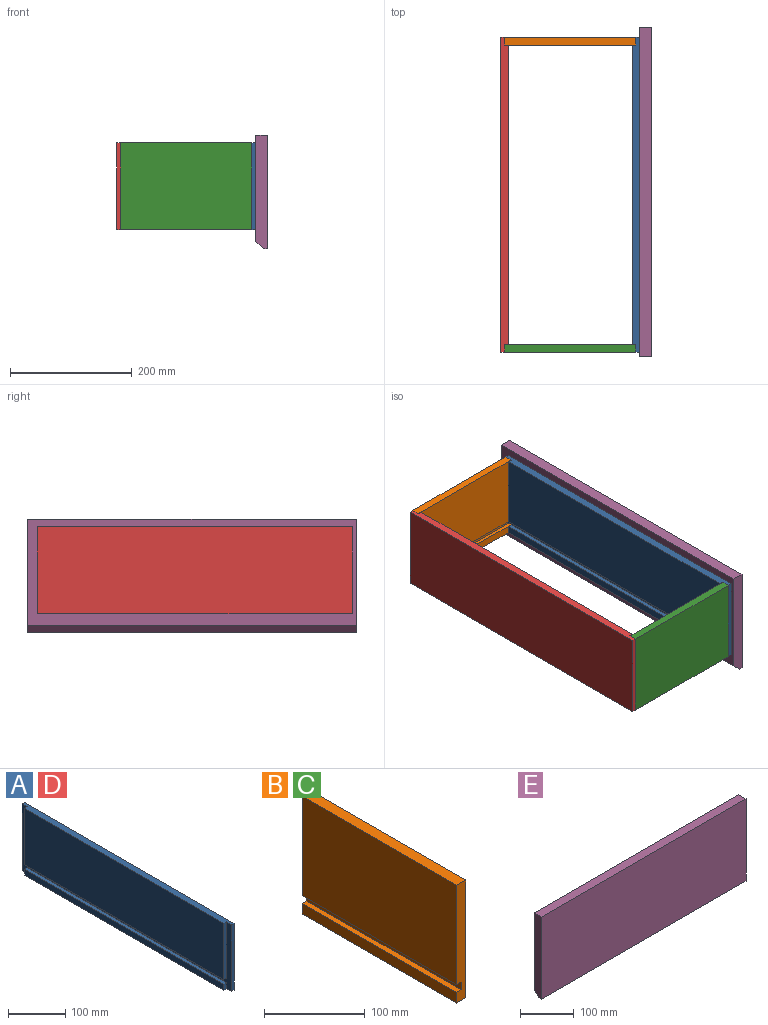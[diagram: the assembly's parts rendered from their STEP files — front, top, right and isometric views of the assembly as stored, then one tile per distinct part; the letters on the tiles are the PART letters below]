
ASSEMBLY  parts=5 mates=4
PART A: 14 faces, bbox 12.7x517.5x142.9 mm
  f0: plane 492.13x12.7mm, normal (-1,0,0), area 6250mm2, adj f6,f9,f10,f12
  f1: plane 120.65x6.35mm, normal (0,-1,0), area 766.1mm2, adj f3,f4,f11,f13
  f2: plane 120.65x6.35mm, normal (0,1,0), area 766.1mm2, adj f3,f4,f11,f13
  f3: plane 517.53x12.7mm, normal (0,0,1), area 6411.3mm2, adj f1,f2,f4,f5,f7,f8,f11
  f4: plane 492.13x120.65mm, normal (-1,0,0), area 59374.9mm2, adj f1,f2,f3,f13
  f5: plane 142.88x6.35mm, normal (0,-1,0), area 907.3mm2, adj f3,f6,f8,f11
  f6: plane 517.53x12.7mm, normal (0,0,-1), area 6411.3mm2, adj f0,f5,f7,f8,f9,f10,f11
  f7: plane 142.88x6.35mm, normal (0,1,0), area 907.3mm2, adj f3,f6,f8,f11
  f8: plane 517.53x142.88mm, normal (1,0,0), area 73941.4mm2, adj f3,f5,f6,f7
  f9: plane 12.7x6.35mm, normal (0,-1,0), area 80.6mm2, adj f0,f6,f11,f12
  f10: plane 12.7x6.35mm, normal (0,1,0), area 80.6mm2, adj f0,f6,f11,f12
  f11: plane 517.53x142.88mm, normal (-1,0,0), area 8316.5mm2, adj f1,f2,f3,f5,f6,f7,f9,f10
  f12: plane 492.13x6.35mm, normal (0,0,1), area 3125mm2, adj f0,f9,f10,f11
  f13: plane 492.13x6.35mm, normal (0,0,-1), area 3125mm2, adj f1,f2,f4,f11
PART B: 10 faces, bbox 12.7x215.9x142.9 mm
  f0: plane 215.9x12.7mm, normal (-1,0,0), area 2741.9mm2, adj f1,f2,f3,f8
  f1: plane 142.88x12.7mm, normal (0,-1,0), area 1754mm2, adj f0,f2,f4,f5,f6,f7,f8,f9
  f2: plane 215.9x12.7mm, normal (0,0,-1), area 2741.9mm2, adj f0,f1,f3,f5
  f3: plane 142.88x12.7mm, normal (0,1,0), area 1754mm2, adj f0,f2,f4,f5,f6,f7,f8,f9
  f4: plane 215.9x12.7mm, normal (0,0,1), area 2741.9mm2, adj f1,f3,f5,f6
  f5: plane 215.9x142.88mm, normal (1,0,0), area 30846.7mm2, adj f1,f2,f3,f4
  f6: plane 215.9x120.65mm, normal (-1,0,0), area 26048.3mm2, adj f1,f3,f4,f7
  f7: plane 215.9x6.35mm, normal (0,0,-1), area 1371mm2, adj f1,f3,f6,f9
  f8: plane 215.9x6.35mm, normal (0,0,1), area 1371mm2, adj f0,f1,f3,f9
  f9: plane 215.9x9.53mm, normal (-1,0,0), area 2056.4mm2, adj f1,f3,f7,f8
PART C: same geometry as B
PART D: same geometry as A
PART E: 7 faces, bbox 539.8x19.1x187.3 mm
  f0: plane 187.33x19.05mm, normal (-1,0,0), area 3487.9mm2, adj f1,f3,f4,f5,f6
  f1: plane 539.75x6.35mm, normal (0,0,-1), area 3427.4mm2, adj f0,f2,f4,f6
  f2: plane 187.33x19.05mm, normal (1,0,0), area 3487.9mm2, adj f1,f3,f4,f5,f6
  f3: plane 539.75x19.05mm, normal (0,0,1), area 10282.2mm2, adj f0,f2,f4,f5
  f4: plane 539.75x187.33mm, normal (0,-1,0), area 101108.7mm2, adj f0,f1,f2,f3
  f5: plane 539.75x174.63mm, normal (0,1,0), area 94253.8mm2, adj f0,f2,f3,f6
  f6: plane 539.75x12.7mm, normal (0,0.71,-0.71), area 9694.2mm2, adj f0,f1,f2,f5
PLACE A rot(axis=(0,0,-1),0deg) t=(-138.5,-435.84,-178.55)mm
PLACE B rot(axis=(0,0,1),90deg) t=(-132.15,68.98,-178.55)mm
PLACE C rot(axis=(0,0,-1),90deg) t=(-348.05,-423.14,-178.55)mm
PLACE D rot(axis=(0,0,-1),180deg) t=(-341.7,81.68,-178.55)mm
PLACE E rot(axis=(0,0,1),90deg) t=(-125.8,-442.19,-210.3)mm
MATE fastened C.f3 <-> A.f11  axis (1,0,0) through (-132.15,-435.84,-35.68)mm
MATE fastened B.f3 <-> D.f11  axis (-1,0,0) through (-348.05,81.68,-35.68)mm
MATE fastened B.f1 <-> A.f11  axis (1,0,0) through (-132.15,81.68,-35.68)mm
MATE fastened A.f8 <-> E.f5  axis (1,0,0) through (-125.8,-177.08,-35.68)mm
